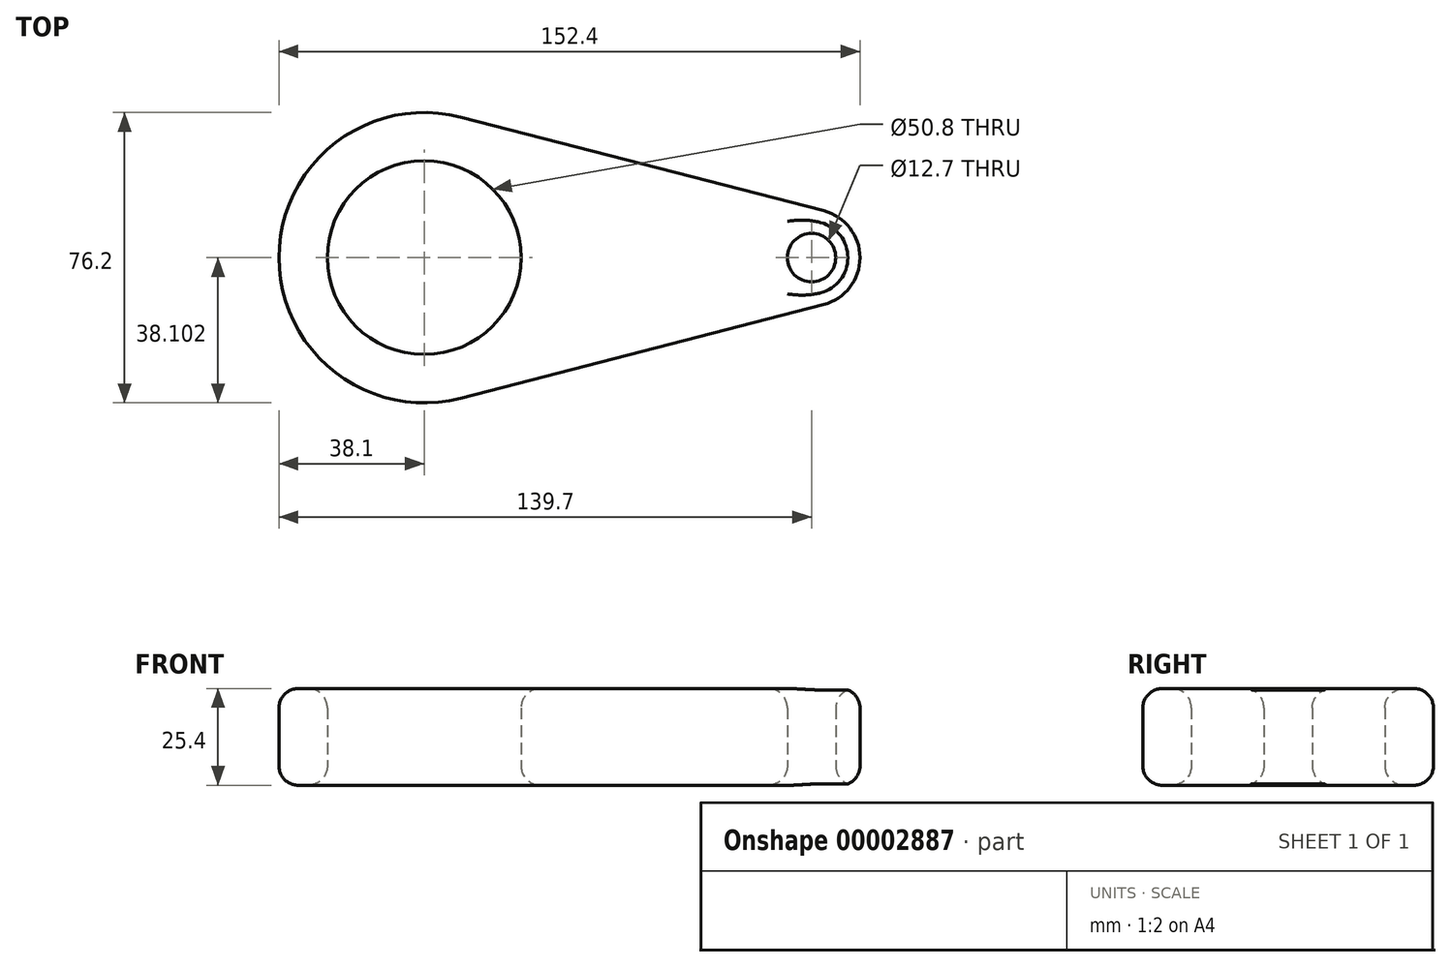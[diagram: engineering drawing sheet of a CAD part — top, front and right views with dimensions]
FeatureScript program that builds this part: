
annotation { "Feature Type Name" : "Feature", "Feature Type Description" : "" }
export const myFeature = defineFeature(function(context is Context, id is Id, definition is map)
    precondition{}
    {
        {
            var Q0;
            Q0=qCreatedBy(makeId("Top.planeOp"),FACE);
            var sketch = newSketch(context, id + "F0", { "sketchPlane" : qUnion([Q0])});
            skCircle(sketch, "E0", {"center": v(-51.02, 21.1) * mm, "radius": 38.1 * mm});
            skCircle(sketch, "E1", {"center": v(50.58, 21.1) * mm, "radius": 12.7 * mm});
            skLineSegment(sketch, "E2", {"start": v(-41.5, 58) * mm, "end": v(53.75, 33.4) * mm});
            skLineSegment(sketch, "E3", {"start": v(-41.5, -15.79) * mm, "end": v(53.75, 8.8) * mm});
            skCircle(sketch, "E4", {"center": v(-51.02, 21.1) * mm, "radius": 25.4 * mm});
            skCircle(sketch, "E5", {"center": v(50.58, 21.1) * mm, "radius": 6.35 * mm});
            skSolve(sketch);
        }
        {
            var Q0;
            {var subQ0=sQuery(id+"F0.wireOp",EDGE,"E0");var subQ2=makeQuery(id+"F0.imprint","INTERSECT",VERTEX,{"derivedFrom":[subQ0,sQuery(id+"F0.wireOp",EDGE,"E2")]});Q0=makeQuery(id+"F0.imprint","IMPRINT",FACE,{"disambiguationData":[TD([[makeQuery(id+"F0.imprint","IMPRINT",EDGE,{"disambiguationData":[TD([[subQ2,-1.0]])],"derivedFrom":subQ0}),1.0]])]});}
            var Q1;
            {var subQ0=sQuery(id+"F0.wireOp",EDGE,"E1");var subQ2=makeQuery(id+"F0.imprint","INTERSECT",VERTEX,{"derivedFrom":[subQ0,sQuery(id+"F0.wireOp",EDGE,"E2")]});Q1=makeQuery(id+"F0.imprint","IMPRINT",FACE,{"disambiguationData":[TD([[makeQuery(id+"F0.imprint","IMPRINT",EDGE,{"disambiguationData":[TD([[subQ2,-1.0]])],"derivedFrom":subQ0}),1.0]])]});}
            var Q2;
            {var subQ1=sQuery(id+"F0.wireOp",EDGE,"E2");Q2=makeQuery(id+"F0.imprint","IMPRINT",FACE,{"disambiguationData":[TD([[makeQuery(id+"F0.imprint","IMPRINT",EDGE,{"derivedFrom":subQ1}),-1.0]])]});}
            extrude(context, id + "F1", {"entities" : qUnion([Q0, Q1, Q2]), "depth" : 25.4 * mm});
        }
        {
            var Q0;
            Q0=makeQuery(id+"F1.opExtrude","CAP_FACE",FACE,{"disambiguationData":[OSD([sQuery(id+"F0.wireOp",EDGE,"E0"),sQuery(id+"F0.wireOp",EDGE,"E1"),sQuery(id+"F0.wireOp",EDGE,"E2"),sQuery(id+"F0.wireOp",EDGE,"E3")])],"isStart":false});
            fillet(context, id + "F2", {"entities" : qUnion([Q0]), "radius" : 5.08 * mm, "tangentPropagation" : true, "allowEdgeOverflow" : false});
        }
        {
            var Q0;
            Q0=makeQuery(id+"F1.opExtrude","CAP_FACE",FACE,{"disambiguationData":[OSD([sQuery(id+"F0.wireOp",EDGE,"E0"),sQuery(id+"F0.wireOp",EDGE,"E1"),sQuery(id+"F0.wireOp",EDGE,"E2"),sQuery(id+"F0.wireOp",EDGE,"E3")])],"isStart":true});
            fillet(context, id + "F3", {"entities" : qUnion([Q0]), "radius" : 5.08 * mm, "tangentPropagation" : true, "allowEdgeOverflow" : false});
        }
    });
